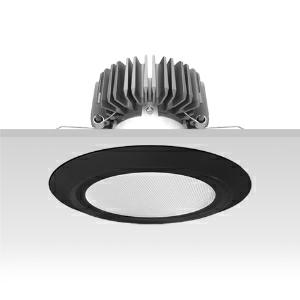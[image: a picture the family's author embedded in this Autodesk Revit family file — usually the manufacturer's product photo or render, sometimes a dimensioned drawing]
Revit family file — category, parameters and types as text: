
# Revit family: 3f_filippi_-_3f_reno_bianco_ampio_3f_filippi_-_30650_a01049_-_3f_reno_200_wh_2000-930_ep_wide___smp_bk_acaa
name_source: partatom
category: Lighting Fixtures
units: mm (PartAtom-declared; Revit-internal decimal feet)

## family parameters
Cut with Voids When Loaded = No
Host = Face
Light Source = No
Part Type = Normal
Room Calculation Point = No
Round Connector Dimension = Use Diameter
Shared = No

## types (1)
- 3F Filippi - 3F Reno Bianco Ampio (1 x LED, 1650 lm, 25 W, 3000 K)
    Apparent Load = 25 VA
    Approval mark = ENEC
    CIE Flux Codes = 74 92 98 100 100
    Color Rendering = 90
    Color Temperature = 3000 K
    Control Gear = Electronic ballast
    Default Elevation = 1800 mm
    Description = ILLUMINOTECHNICAL
Luminous efficiency 100% (DLOR 100%, ULOR 0%).
Initial luminous flux of the luminaire 1650 lm.
Emergency luminaire luminous flux BLF 16.7%.
Direct symmetric wide distribution.
Installation Interdistance Transv.D = 1.06 x hu - Long.D = 1.04 x hu.
Average luminance <3000 cd/m² for radial angles >65°.
Tabular UGR (CIE 117 - 4H-8H; S=0.25H; 70/50/20): RUG 21.3 - 21.1.
Beam angle: 70° - 69°.
Luminous efficacy 66 lm/W.
Lifetime (L90/B10): 30000 h. (tq+25°C)
Lifetime (L85/B10): 50000 h. (tq+25°C)
Lifetime (L70/B10): 80000 h. (tq+25°C)
Sudden decreased luminous flux after 50000 hours: 0% (C0).
Photobiological safety in compliance with IEC/TR 62778: RG0 risk exempt, (IEC 62471).
In compliance with IEC/EN 62722-2-1 - IEC/EN 62717 standards.

SOURCE
Compact LED module 2000/930.
Energy efficiency class (UE 2019/2020 - UE 2019/2015): E.
CIE 13.3 Colour rendering index: CRI >90 (R9 >50%).
IES TM-30 Fidelity Index: Rf = 92 Rg = 101.
CCT nominal colour temperature 3000 K.
Colour initial tolerance (MacAdam): SDCM 3.
Zhaga Book 3 compliant.

MECHANICAL
Passive heat dissipator in die-casting aluminium, oversized, for optimum thermal management of the LED module.
Parabolic element with graduated/concentric rings in white polycarbonate.
Transparent external lens with glossy and satin differentiated surfaces, with a cooling and anti-insect system in methacrylate (PMMA).
Fastening spring clips in stainless steel.
Dimensions: diameter 226 mm, height 146 mm. Weight 1.555 kg.
IP44 protection degree for exposed part, IP20 for recessed part.
Mechanical strength to impacts IK05 (0.7 joule).
Glow-wire test resistance 650°C.

ELECTRICAL
Wiring on a separate unit.
Halogen Free electronic wiring 230V-50/60Hz, power factor 0.90, THD <25%, constant output current, SELV, class II, 1 driver.
Power of the luminaire 25 W.
CE - IEC 60598-1 - EN 60598-1.
EP maintained emergency wiring on board, 1h duration, 24h recharge; compliant with EN 60598-2-22, excluding high risk areas.
SAFE FLICKER: PstLM=<1 and SVM=<0.4 (IEC TR 61547-1 and IEC TR 63158), to ensure a more comfortable and safe light.
Ambient temperature from +5°C to +25°C.
Temperature class T6 max 85°C.
Relative humidity UR: <85%.

INSTALLATION
Pull-up recessed fitting.
False ceiling carving: 200 mm.
All accessories dedicated to this product are available on the Catalog and on our website www.3F-Filippi.com.

ACCESSORIES
A01049 - Anti-glare microprismatic SMP diffuser in methacrylate (PMMA), locked and in line with the trim, in black polycarbonate.

APPLICATIONS
Suitable product for food production plants (HACCP), IFS (Food Version 6), BRC (GSFS Food Version 7).
Environments: architectural, commercial, exhibition areas, transit areas, corridors, shops, display windows, service areas.
In false ceilings with narrow voids.

WARNING
Luminaire designed for disposal/recycling at end-of-life.
Replaceable (LED only) light source by a professional. Replaceable control gear by a professional.
    Height = 0 mm  [stored 0 ft]
    Lamp = 1 x LED
    Lamp Light Flux = 1650 lm
    Lamp Power = 25 W
    Lamp count = 1
    Length = 226 mm
    Lifetime = 50000 h
    Luminous efficacy = 66 lm/W
    Manufacturer = 3F Filippi
    ModVariant = No
    Model = 3F Filippi - 30650+A01049 - 3F Reno 200 WH 2000-930 EP WIDE + SMP BK
    Mounting Place = Ceiling
    Mounting Type = Recessed
    Number of Poles = 1
    OnlyDefault = Yes
    Power Factor = 1
    Product Name = 3F Filippi - 3F Reno Bianco Ampio
    Product group = recessed luminaire
    ProductGroupID = 4
    Protection Class = Protection class II
    Protection Degree = IP 20
    RLX_Detail_Level = 1
    RLX_Emergency_Light_Flux = 0 lm
    RLX_Emergency_Type = 0
    RLX_Emergency_Type_DB = No
    RlxData = <blob elided: 97145 chars, md5=3a5731c1>
    Socket = socket
    Standby Power = 0 W
    System Light Flux = 1650 lm
    System Power = 25 W
    Type Comments = Product without accessories
    Type Image = 3ffilippi_3f_reno_200_bk_vs_smp.jpg
    URL = http://relux.com
    VarID = ---
    Voltage = 0 V
    Weight = 0.00 kg
    Width = 0 mm  [stored 0 ft]

note: [stored X ft] marks values corroborated as IEEE doubles in the binary element streams (Revit-internal decimal feet)

## geometry (parser evidence)
native form markers: Blend x4, Sweep x11
no freeform markers — native parametric forms only
